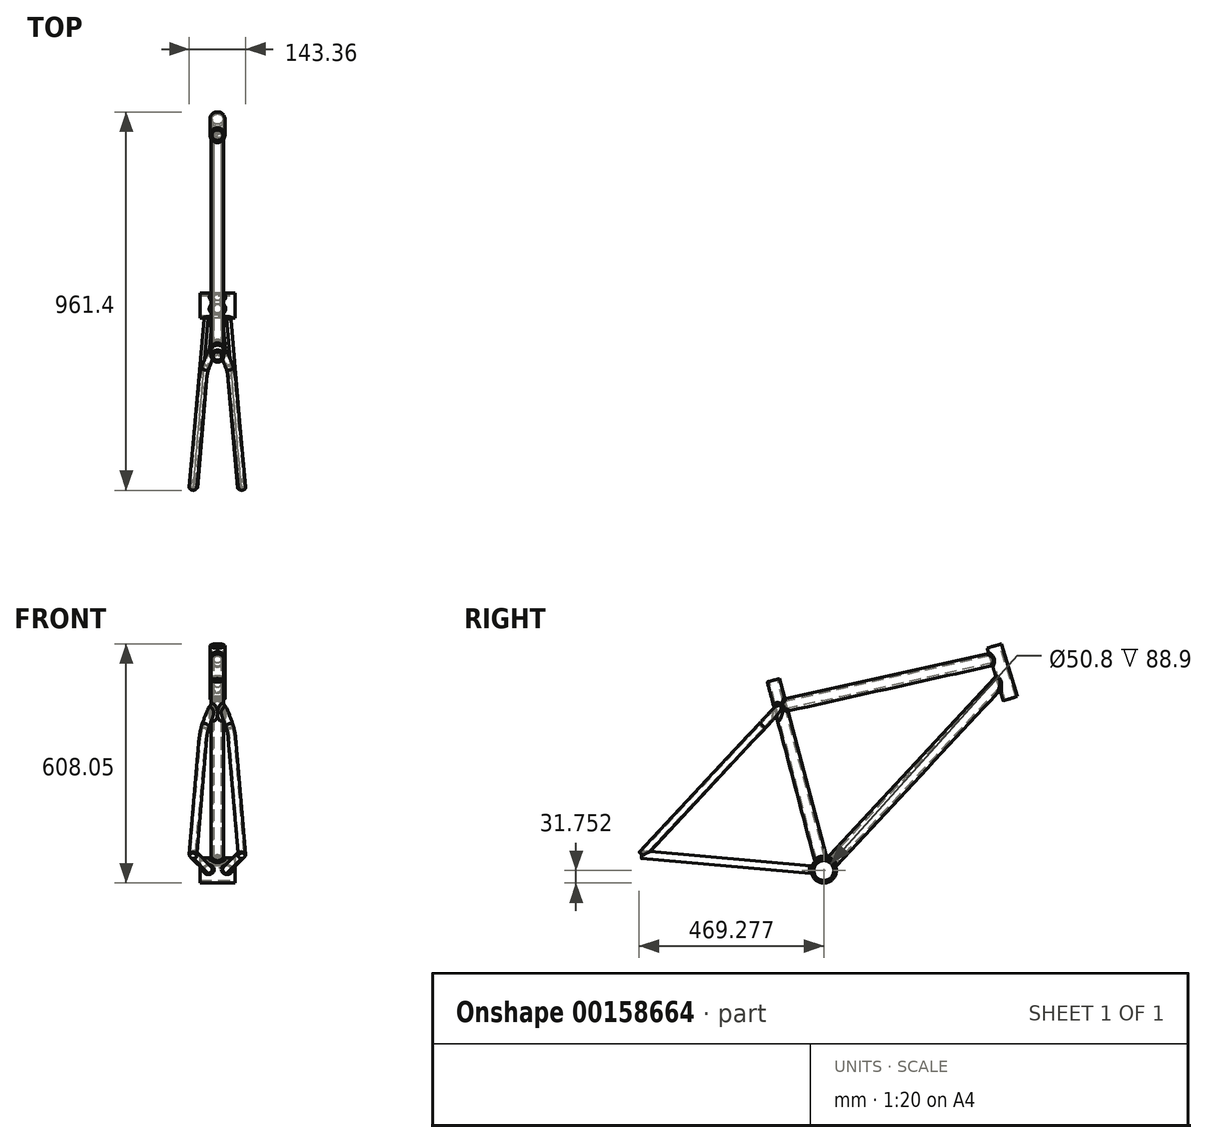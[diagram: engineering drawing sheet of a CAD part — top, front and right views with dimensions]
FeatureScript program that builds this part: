
annotation { "Feature Type Name" : "Feature", "Feature Type Description" : "" }
export const myFeature = defineFeature(function(context is Context, id is Id, definition is map)
    precondition{}
    {
        {
            var Q0;
            Q0=qCreatedBy(makeId("Right.planeOp"),FACE);
            var sketch = newSketch(context, id + "F0", { "sketchPlane" : qUnion([Q0])});
            skLineSegment(sketch, "E0", {"start": v(40.66, 113.91) * mm, "end": v(81.5, -19.68) * mm});
            skLineSegment(sketch, "E1.bottom", {"start": v(22.44, 108.34) * mm, "end": v(58.88, 119.48) * mm});
            skLineSegment(sketch, "E1.top", {"start": v(63.29, -25.25) * mm, "end": v(99.72, -14.11) * mm});
            skLineSegment(sketch, "E1.left", {"start": v(22.44, 108.34) * mm, "end": v(63.29, -25.25) * mm});
            skLineSegment(sketch, "E1.right", {"start": v(58.88, 119.48) * mm, "end": v(99.72, -14.11) * mm});
            skLineSegment(sketch, "E2", {"start": v(49.94, 83.55) * mm, "end": v(-503.21, -39.48) * mm});
            skLineSegment(sketch, "E3", {"start": v(-503.21, -39.48) * mm, "end": v(-392.4, -456.82) * mm});
            skLineSegment(sketch, "E4", {"start": v(-392.4, -456.82) * mm, "end": v(64.8, 34.97) * mm});
            skCircle(sketch, "E5", {"center": v(-392.4, -456.82) * mm, "radius": 31.75 * mm});
            skLineSegment(sketch, "E6", {"start": v(-503.21, -39.48) * mm, "end": v(-520.8, 26.74) * mm});
            skLineSegment(sketch, "E7", {"start": v(-520.8, 26.74) * mm, "end": v(-536.14, 22.67) * mm});
            skLineSegment(sketch, "E8.0", {"start": v(-536.14, 22.67) * mm, "end": v(-407.6, -461.46) * mm});
            skLineSegment(sketch, "E9", {"start": v(-407.6, -461.46) * mm, "end": v(-392.4, -456.82) * mm});
            skSolve(sketch);
        }
        {
            var Q0;
            {var subQ4=sQuery(id+"F0.wireOp",EDGE,"E6");Q0=makeQuery(id+"F0.imprint","IMPRINT",FACE,{"disambiguationData":[TD([[makeQuery(id+"F0.imprint","IMPRINT",EDGE,{"derivedFrom":subQ4}),1.0]])]});}
            var Q1;
            {var subQ0=sQuery(id+"F0.wireOp",EDGE,"E9");Q1=makeQuery(id+"F0.imprint","IMPRINT",FACE,{"disambiguationData":[TD([[makeQuery(id+"F0.imprint","IMPRINT",EDGE,{"derivedFrom":subQ0}),1.0]])]});}
            var Q2;
            Q2=sQuery(id+"F0.wireOp",EDGE,"E3");
            revolve(context, id + "F1", {"entities" : qUnion([Q0, Q1]), "axis" : qUnion([Q2]), "revolveType" : RevolveType.FULL});
        }
        {
            var Q0;
            {var subQ0=sQuery(id+"F0.wireOp",EDGE,"E2");var subQ1=sQuery(id+"F0.wireOp",EDGE,"E0");var subQ2=makeQuery(id+"F0.imprint","INTERSECT",VERTEX,{"derivedFrom":[subQ1,subQ0]});Q0=makeQuery(id+"F0.imprint","IMPRINT",FACE,{"disambiguationData":[TD([[makeQuery(id+"F0.imprint","IMPRINT",EDGE,{"disambiguationData":[TD([[subQ2,-1.0]])],"derivedFrom":subQ1}),-1.0]])]});}
            var Q1;
            {var subQ0=sQuery(id+"F0.wireOp",EDGE,"E1.bottom");var subQ1=sQuery(id+"F0.wireOp",EDGE,"E0");var subQ2=makeQuery(id+"F0.imprint","INTERSECT",VERTEX,{"derivedFrom":[subQ1,subQ0]});Q1=makeQuery(id+"F0.imprint","IMPRINT",FACE,{"disambiguationData":[TD([[makeQuery(id+"F0.imprint","IMPRINT",EDGE,{"disambiguationData":[TD([[subQ2,-1.0]])],"derivedFrom":subQ1}),-1.0]])]});}
            var Q2;
            {var subQ0=sQuery(id+"F0.wireOp",EDGE,"E1.top");var subQ1=sQuery(id+"F0.wireOp",EDGE,"E0");var subQ2=makeQuery(id+"F0.imprint","INTERSECT",VERTEX,{"derivedFrom":[subQ1,subQ0]});Q2=makeQuery(id+"F0.imprint","IMPRINT",FACE,{"disambiguationData":[TD([[makeQuery(id+"F0.imprint","IMPRINT",EDGE,{"disambiguationData":[TD([[subQ2,1.0]])],"derivedFrom":subQ1}),-1.0]])]});}
            var Q3;
            Q3=sQuery(id+"F0.wireOp",EDGE,"E0");
            revolve(context, id + "F2", {"entities" : qUnion([Q0, Q1, Q2]), "axis" : qUnion([Q3]), "revolveType" : RevolveType.FULL});
        }
        {
            var Q0;
            {var subQ0=sQuery(id+"F0.wireOp",EDGE,"E9");Q0=makeQuery(id+"F0.imprint","IMPRINT",FACE,{"disambiguationData":[TD([[makeQuery(id+"F0.imprint","IMPRINT",EDGE,{"derivedFrom":subQ0}),1.0]])]});}
            var Q1;
            {var subQ0=sQuery(id+"F0.wireOp",EDGE,"E4");var subQ3=sQuery(id+"F0.wireOp",EDGE,"E5");var subQ5=makeQuery(id+"F0.imprint","INTERSECT",VERTEX,{"derivedFrom":[subQ0,subQ3]});Q1=makeQuery(id+"F0.imprint","IMPRINT",FACE,{"disambiguationData":[TD([[makeQuery(id+"F0.imprint","IMPRINT",EDGE,{"disambiguationData":[TD([[subQ5,-1.0]])],"derivedFrom":subQ3}),1.0]])]});}
            var Q2;
            {var subQ0=sQuery(id+"F0.wireOp",EDGE,"E9");Q2=makeQuery(id+"F0.imprint","IMPRINT",FACE,{"disambiguationData":[TD([[makeQuery(id+"F0.imprint","IMPRINT",EDGE,{"derivedFrom":subQ0}),-1.0]])]});}
            var Q3;
            Q3=sQuery(id+"F0.wireOp",EDGE,"E5");
            extrude(context, id + "F3", {"entities" : qUnion([Q0, Q1, Q2]), "surfaceEntities" : qUnion([Q3]), "endBound" : BoundingType.SYMMETRIC, "depth" : 88.9 * mm});
        }
        {
            var Q0;
            Q0=sQuery(id+"F0.wireOp",VERTEX,"E2.start");
            var Q1;
            Q1=sQuery(id+"F0.wireOp",EDGE,"E2");
            cPlane(context, id + "F4", {"entities" : qUnion([Q0, Q1]), "cplaneType" : CPlaneType.LINE_POINT, "offset" : 25.4 * mm, "width" : 152.4 * mm, "height" : 152.4 * mm});
        }
        {
            var Q0;
            Q0=qCreatedBy(id+"F4.planeOp",FACE);
            var sketch = newSketch(context, id + "F5", { "sketchPlane" : qUnion([Q0])});
            skCircle(sketch, "E10", {"center": v(0, 70.71) * mm, "radius": 15.88 * mm});
            skCircle(sketch, "E11", {"center": v(0, 70.71) * mm, "radius": 9.52 * mm});
            skSolve(sketch);
        }
        {
            var Q0;
            Q0=makeQuery(id+"F5.imprint","IMPRINT",FACE,{"disambiguationData":[TD([[makeQuery(id+"F5.imprint","IMPRINT",EDGE,{"derivedFrom":sQuery(id+"F5.wireOp",EDGE,"E10")}),1.0]])]});
            var Q1;
            Q1=sQuery(id+"F0.wireOp",EDGE,"E2");
            sweep(context, id + "F6", {"operationType" : NewBodyOperationType.ADD, "profiles" : qUnion([Q0]), "path" : qUnion([Q1])});
        }
        {
            var Q0;
            Q0=sQuery(id+"F0.wireOp",VERTEX,"E4.end");
            var Q1;
            Q1=sQuery(id+"F0.wireOp",EDGE,"E4");
            cPlane(context, id + "F7", {"entities" : qUnion([Q0, Q1]), "cplaneType" : CPlaneType.LINE_POINT, "offset" : 25.4 * mm, "width" : 152.4 * mm, "height" : 152.4 * mm});
        }
        {
            var Q0;
            Q0=qCreatedBy(id+"F7.planeOp",FACE);
            var sketch = newSketch(context, id + "F8", { "sketchPlane" : qUnion([Q0])});
            skCircle(sketch, "E12", {"center": v(0, 23.65) * mm, "radius": 15.88 * mm});
            skCircle(sketch, "E13", {"center": v(0, 23.65) * mm, "radius": 9.52 * mm});
            skSolve(sketch);
        }
        {
            var Q0;
            Q0=makeQuery(id+"F8.imprint","IMPRINT",FACE,{"disambiguationData":[TD([[makeQuery(id+"F8.imprint","IMPRINT",EDGE,{"derivedFrom":sQuery(id+"F8.wireOp",EDGE,"E12")}),1.0]])]});
            var Q1;
            Q1=sQuery(id+"F0.wireOp",EDGE,"E4");
            sweep(context, id + "F9", {"operationType" : NewBodyOperationType.ADD, "profiles" : qUnion([Q0]), "path" : qUnion([Q1])});
        }
        {
            var Q0;
            Q0=qCreatedBy(makeId("Front.planeOp"),FACE);
            cPlane(context, id + "F10", {"entities" : qUnion([Q0]), "cplaneType" : CPlaneType.OFFSET, "offset" : 392.4 * mm, "width" : 152.4 * mm, "height" : 152.4 * mm});
        }
        {
            var Q0;
            Q0=qCreatedBy(id+"F10.planeOp",FACE);
            var sketch = newSketch(context, id + "F11", { "sketchPlane" : qUnion([Q0])});
            skLineSegment(sketch, "E14", {"start": v(44.45, -456.82) * mm, "end": v(-46.66, -456.82) * mm});
            skSolve(sketch);
        }
        {
            var Q0;
            Q0=qCreatedBy(id+"F10.planeOp",FACE);
            var Q1;
            Q1=sQuery(id+"F11.wireOp",EDGE,"E14");
            cPlane(context, id + "F12", {"entities" : qUnion([Q0, Q1]), "cplaneType" : CPlaneType.LINE_ANGLE, "offset" : 25.4 * mm, "angle" : 275 * degree, "width" : 152.4 * mm, "height" : 152.4 * mm});
        }
        {
            var Q0;
            Q0=qCreatedBy(id+"F12.planeOp",FACE);
            var sketch = newSketch(context, id + "F13", { "sketchPlane" : qUnion([Q0])});
            skLineSegment(sketch, "E15", {"start": v(33.46, -382.85) * mm, "end": v(23.9, -382.85) * mm});
            skLineSegment(sketch, "E16", {"start": v(30.7, -351.1) * mm, "end": v(71.02, -814.65) * mm});
            skLineSegment(sketch, "E17", {"start": v(0.57, -382.85) * mm, "end": v(0.57, -884.07) * mm});
            skLineSegment(sketch, "E18.0", {"start": v(21.14, -351.1) * mm, "end": v(61.53, -815.47) * mm});
            skLineSegment(sketch, "E19", {"start": v(71.02, -814.65) * mm, "end": v(61.53, -815.47) * mm});
            skLineSegment(sketch, "E20.MirrorCS", {"start": v(-20, -351.1) * mm, "end": v(-60.4, -815.47) * mm});
            skLineSegment(sketch, "E21.MirrorCS", {"start": v(-69.88, -814.65) * mm, "end": v(-60.4, -815.47) * mm});
            skLineSegment(sketch, "E22.MirrorCS", {"start": v(-29.56, -351.1) * mm, "end": v(-69.88, -814.65) * mm});
            skLineSegment(sketch, "E23", {"start": v(30.7, -351.1) * mm, "end": v(21.14, -351.1) * mm});
            skPoint(sketch, "E24.orphan", {"position": v(33.46, -382.85) * mm});
            skPoint(sketch, "E25.orphan", {"position": v(23.9, -382.85) * mm});
            skPoint(sketch, "E26.orphan", {"position": v(-32.32, -382.85) * mm});
            skPoint(sketch, "E27.orphan", {"position": v(-22.76, -382.85) * mm});
            skPoint(sketch, "E28.trimOffspring.end.orphan", {"position": v(-44.45, -382.85) * mm});
            skLineSegment(sketch, "E29.trimOffspring", {"start": v(-20, -351.1) * mm, "end": v(-29.56, -351.1) * mm});
            skPoint(sketch, "E30.orphan", {"position": v(45.59, -382.85) * mm});
            skSolve(sketch);
        }
        {
            var Q0;
            {var subQ0=sQuery(id+"F13.wireOp",EDGE,"E16");Q0=makeQuery(id+"F13.imprint","IMPRINT",FACE,{"disambiguationData":[TD([[makeQuery(id+"F13.imprint","IMPRINT",EDGE,{"derivedFrom":subQ0}),-1.0]])]});}
            var Q1;
            Q1=sQuery(id+"F13.wireOp",EDGE,"E18.0");
            revolve(context, id + "F14", {"operationType" : NewBodyOperationType.ADD, "entities" : qUnion([Q0]), "axis" : qUnion([Q1]), "revolveType" : RevolveType.FULL});
        }
        {
            var Q0;
            Q0=makeQuery(id+"F13.imprint","IMPRINT",FACE,{"disambiguationData":[TD([[makeQuery(id+"F13.imprint","IMPRINT",EDGE,{"derivedFrom":sQuery(id+"F13.wireOp",EDGE,"E20.MirrorCS")}),-1.0]])]});
            var Q1;
            Q1=sQuery(id+"F13.wireOp",EDGE,"E20.MirrorCS");
            revolve(context, id + "F15", {"operationType" : NewBodyOperationType.ADD, "entities" : qUnion([Q0]), "axis" : qUnion([Q1]), "revolveType" : RevolveType.FULL});
        }
        {
            var Q0;
            Q0=sQuery(id+"F13.wireOp",VERTEX,"E19.end");
            var Q1;
            Q1=sQuery(id+"F0.wireOp",VERTEX,"E3.start");
            var Q2;
            Q2=sQuery(id+"F13.wireOp",VERTEX,"E20.MirrorCS.end");
            cPlane(context, id + "F16", {"entities" : qUnion([Q0, Q1, Q2]), "cplaneType" : CPlaneType.THREE_POINT, "offset" : 25.4 * mm, "width" : 152.4 * mm, "height" : 152.4 * mm});
        }
        {
            var Q0;
            Q0=qCreatedBy(id+"F16.planeOp",FACE);
            var sketch = newSketch(context, id + "F17", { "sketchPlane" : qUnion([Q0])});
            skPoint(sketch, "E31.0", {"position": v(-61.53, -887.79) * mm});
            skPoint(sketch, "E32.0", {"position": v(60.4, -887.79) * mm});
            skPoint(sketch, "E33.0", {"position": v(0, -372.24) * mm});
            skLineSegment(sketch, "E34", {"start": v(-36.13, -481.84) * mm, "end": v(-61.53, -887.79) * mm});
            skLineSegment(sketch, "E35", {"start": v(51.14, -372.24) * mm, "end": v(-6.35, -372.24) * mm});
            skPoint(sketch, "E36.visualSharp", {"position": v(-34.83, -461.14) * mm});
            skArc(sketch, "E36.filletArc", {"start": v(-30.2, -440.93) * mm, "mid": v(-34, -461.26) * mm, "end": v(-36.13, -481.84) * mm});
            skFitSpline(sketch, "E37", {"points": [v(-30.2, -440.93) * mm, v(-19.06, -399.88) * mm, v(-12.73, -381.3) * mm, v(-6.35, -372.24) * mm], "startDerivative": vector(26.27, 97.47) * mm, "endDerivative": vector(29.13, 35.48) * mm});
            skSolve(sketch);
        }
        {
            var Q0;
            Q0=sQuery(id+"F17.wireOp",VERTEX,"E31.0");
            var Q1;
            Q1=sQuery(id+"F17.wireOp",EDGE,"E34");
            cPlane(context, id + "F18", {"entities" : qUnion([Q0, Q1]), "cplaneType" : CPlaneType.LINE_POINT, "offset" : 25.4 * mm, "width" : 152.4 * mm, "height" : 152.4 * mm});
        }
        {
            var Q0;
            Q0=qCreatedBy(id+"F18.planeOp",FACE);
            var sketch = newSketch(context, id + "F19", { "sketchPlane" : qUnion([Q0])});
            skCircle(sketch, "E38", {"center": v(6.6, 340.53) * mm, "radius": 9.53 * mm});
            skCircle(sketch, "E39", {"center": v(6.6, 340.53) * mm, "radius": 6.35 * mm});
            skSolve(sketch);
        }
        {
            var Q0;
            Q0=makeQuery(id+"F19.imprint","IMPRINT",FACE,{"disambiguationData":[TD([[makeQuery(id+"F19.imprint","IMPRINT",EDGE,{"derivedFrom":sQuery(id+"F19.wireOp",EDGE,"E38")}),1.0]])]});
            var Q1;
            Q1=sQuery(id+"F17.wireOp",EDGE,"E34");
            var Q2;
            Q2=sQuery(id+"F17.wireOp",EDGE,"E36.filletArc");
            var Q3;
            Q3=sQuery(id+"F17.wireOp",EDGE,"E37");
            sweep(context, id + "F20", {"operationType" : NewBodyOperationType.ADD, "profiles" : qUnion([Q0]), "path" : qUnion([Q1, Q2, Q3])});
        }
        {
            var Q0;
            Q0=makeQuery(id+"F1.opRevolve","SWEPT_BODY",BODY,{"disambiguationData":[OSD([sQuery(id+"F0.wireOp",EDGE,"E3"),sQuery(id+"F0.wireOp",EDGE,"E6"),sQuery(id+"F0.wireOp",EDGE,"E7"),sQuery(id+"F0.wireOp",EDGE,"E8.0"),sQuery(id+"F0.wireOp",EDGE,"E9")])]});
            var Q1;
            Q1=qCreatedBy(makeId("Right.planeOp"),FACE);
            mirror(context, id + "F21", {"operationType" : NewBodyOperationType.ADD, "entities" : qUnion([Q0]), "mirrorPlane" : qUnion([Q1])});
        }
        {
            var Q0;
            Q0=makeQuery(id+"F3.opExtrude","CAP_FACE",FACE,{"disambiguationData":[OSD([sQuery(id+"F0.wireOp",EDGE,"E5")])],"isStart":false});
            var sketch = newSketch(context, id + "F22", { "sketchPlane" : qUnion([Q0])});
            skCircle(sketch, "E40.0", {"center": v(-392.4, -456.82) * mm, "radius": 31.75 * mm});
            skCircle(sketch, "E41.0", {"center": v(-392.4, -456.82) * mm, "radius": 25.4 * mm});
            skSolve(sketch);
        }
        {
            var Q0;
            Q0=makeQuery(id+"F22.imprint","IMPRINT",FACE,{"disambiguationData":[TD([[makeQuery(id+"F22.imprint","IMPRINT",EDGE,{"derivedFrom":sQuery(id+"F22.wireOp",EDGE,"E41.0")}),1.0]])]});
            extrude(context, id + "F23", {"entities" : qUnion([Q0]), "operationType" : NewBodyOperationType.REMOVE, "endBound" : BoundingType.THROUGH_ALL, "oppositeDirection" : true, "depth" : 25.4 * mm});
        }
        {
            var Q0;
            Q0=makeQuery(id+"F1.opRevolve","SWEPT_FACE",FACE,{"disambiguationData":[OSD([sQuery(id+"F0.wireOp",EDGE,"E7")])]});
            var sketch = newSketch(context, id + "F24", { "sketchPlane" : qUnion([Q0])});
            skCircle(sketch, "E42.0", {"center": v(0, -496.5) * mm, "radius": 15.87 * mm});
            skCircle(sketch, "E43", {"center": v(0, -496.5) * mm, "radius": 10.8 * mm});
            skSolve(sketch);
        }
        {
            var Q0;
            Q0=makeQuery(id+"F24.imprint","IMPRINT",FACE,{"disambiguationData":[TD([[makeQuery(id+"F24.imprint","IMPRINT",EDGE,{"derivedFrom":sQuery(id+"F24.wireOp",EDGE,"E43")}),1.0]])]});
            var Q1;
            Q1=makeQuery(id+"F3.opExtrude","SWEPT_FACE",FACE,{"disambiguationData":[OSD([sQuery(id+"F0.wireOp",EDGE,"E5")])]});
            extrude(context, id + "F25", {"entities" : qUnion([Q0]), "operationType" : NewBodyOperationType.REMOVE, "endBound" : BoundingType.UP_TO_SURFACE, "oppositeDirection" : true, "endBoundEntityFace" : qUnion([Q1]), "depth" : 25.4 * mm});
        }
        {
            var Q0;
            Q0=makeQuery(id+"F2.opRevolve","SWEPT_FACE",FACE,{"disambiguationData":[OSD([sQuery(id+"F0.wireOp",EDGE,"E1.bottom")])]});
            var sketch = newSketch(context, id + "F26", { "sketchPlane" : qUnion([Q0])});
            skCircle(sketch, "E44", {"center": v(0, 72.19) * mm, "radius": 13.97 * mm});
            skSolve(sketch);
        }
        {
            var Q0;
            Q0=makeQuery(id+"F26.imprint","IMPRINT",FACE,{"disambiguationData":[TD([[makeQuery(id+"F26.imprint","IMPRINT",EDGE,{"derivedFrom":sQuery(id+"F26.wireOp",EDGE,"E44")}),1.0]])]});
            extrude(context, id + "F27", {"entities" : qUnion([Q0]), "operationType" : NewBodyOperationType.REMOVE, "endBound" : BoundingType.THROUGH_ALL, "oppositeDirection" : true, "depth" : 25.4 * mm});
        }
        {
            var Q0;
            Q0=makeQuery(id+"F6.boolean.opBoolean","INTERSECT",EDGE,{"disambiguationData":[OD(1.0)],"derivedFrom":[makeQuery(id+"F1.opRevolve","SWEPT_FACE",FACE,{"disambiguationData":[OSD([sQuery(id+"F0.wireOp",EDGE,"E8.0")])]}),makeQuery(id+"F6.opSweep","SWEPT_FACE",FACE,{"disambiguationData":[OSD([sQuery(id+"F0.wireOp",EDGE,"E2"),sQuery(id+"F5.wireOp",EDGE,"E10")])]})]});
            var Q1;
            Q1=makeQuery(id+"F6.boolean.opBoolean","INTERSECT",EDGE,{"disambiguationData":[OD(0.0)],"derivedFrom":[makeQuery(id+"F1.opRevolve","SWEPT_FACE",FACE,{"disambiguationData":[OSD([sQuery(id+"F0.wireOp",EDGE,"E8.0")])]}),makeQuery(id+"F6.opSweep","SWEPT_FACE",FACE,{"disambiguationData":[OSD([sQuery(id+"F0.wireOp",EDGE,"E2"),sQuery(id+"F5.wireOp",EDGE,"E10")])]})]});
            var Q2;
            Q2=makeQuery(id+"F9.boolean.opBoolean","INTERSECT",EDGE,{"derivedFrom":[makeQuery(id+"F3.opExtrude","SWEPT_FACE",FACE,{"disambiguationData":[OSD([sQuery(id+"F0.wireOp",EDGE,"E5")])]}),makeQuery(id+"F9.opSweep","SWEPT_FACE",FACE,{"disambiguationData":[OSD([sQuery(id+"F0.wireOp",EDGE,"E4"),sQuery(id+"F8.wireOp",EDGE,"E12")])]})]});
            var Q3;
            Q3=makeQuery(id+"F9.boolean.opBoolean","INTERSECT",EDGE,{"derivedFrom":[makeQuery(id+"F3.opExtrude","SWEPT_FACE",FACE,{"disambiguationData":[OSD([sQuery(id+"F0.wireOp",EDGE,"E5")])]}),makeQuery(id+"F6.boolean.opBoolean","SPLIT",FACE,{"disambiguationData":[TD([makeQuery(id+"F1.opRevolve","SWEPT_FACE",FACE,{"disambiguationData":[OSD([sQuery(id+"F0.wireOp",EDGE,"E7")])]})])],"derivedFrom":makeQuery(id+"F1.opRevolve","SWEPT_FACE",FACE,{"disambiguationData":[OSD([sQuery(id+"F0.wireOp",EDGE,"E8.0")])]})})]});
            var Q4;
            {var subQ0=sQuery(id+"F0.wireOp",EDGE,"E5");Q4=makeQuery(id+"F14.boolean.opBoolean","INTERSECT",EDGE,{"derivedFrom":[makeQuery(id+"F9.boolean.opBoolean","SPLIT",FACE,{"disambiguationData":[TD([makeQuery(id+"F1.opRevolve","SWEPT_FACE",FACE,{"disambiguationData":[OSD([sQuery(id+"F0.wireOp",EDGE,"E8.0")])]})])],"derivedFrom":makeQuery(id+"F3.opExtrude","SWEPT_FACE",FACE,{"disambiguationData":[OSD([subQ0])]})}),makeQuery(id+"F14.opRevolve","SWEPT_FACE",FACE,{"disambiguationData":[OSD([sQuery(id+"F13.wireOp",EDGE,"E16")])]})]});}
            var Q5;
            {var subQ0=sQuery(id+"F0.wireOp",EDGE,"E5");Q5=makeQuery(id+"F15.boolean.opBoolean","INTERSECT",EDGE,{"derivedFrom":[makeQuery(id+"F9.boolean.opBoolean","SPLIT",FACE,{"disambiguationData":[TD([makeQuery(id+"F1.opRevolve","SWEPT_FACE",FACE,{"disambiguationData":[OSD([sQuery(id+"F0.wireOp",EDGE,"E8.0")])]})])],"derivedFrom":makeQuery(id+"F3.opExtrude","SWEPT_FACE",FACE,{"disambiguationData":[OSD([subQ0])]})}),makeQuery(id+"F15.opRevolve","SWEPT_FACE",FACE,{"disambiguationData":[OSD([sQuery(id+"F13.wireOp",EDGE,"E22.MirrorCS")])]})]});}
            var Q6;
            {var subQ0=sQuery(id+"F0.wireOp",EDGE,"E5");Q6=makeQuery(id+"F21.opPattern","COPY",EDGE,{"derivedFrom":makeQuery(id+"F14.boolean.opBoolean","INTERSECT",EDGE,{"derivedFrom":[makeQuery(id+"F9.boolean.opBoolean","SPLIT",FACE,{"disambiguationData":[TD([makeQuery(id+"F1.opRevolve","SWEPT_FACE",FACE,{"disambiguationData":[OSD([sQuery(id+"F0.wireOp",EDGE,"E8.0")])]})])],"derivedFrom":makeQuery(id+"F3.opExtrude","SWEPT_FACE",FACE,{"disambiguationData":[OSD([subQ0])]})}),makeQuery(id+"F14.opRevolve","SWEPT_FACE",FACE,{"disambiguationData":[OSD([sQuery(id+"F13.wireOp",EDGE,"E16")])]})]}),"instanceName":"1"});}
            var Q7;
            {var subQ0=sQuery(id+"F0.wireOp",EDGE,"E5");Q7=makeQuery(id+"F21.opPattern","COPY",EDGE,{"derivedFrom":makeQuery(id+"F15.boolean.opBoolean","INTERSECT",EDGE,{"derivedFrom":[makeQuery(id+"F9.boolean.opBoolean","SPLIT",FACE,{"disambiguationData":[TD([makeQuery(id+"F1.opRevolve","SWEPT_FACE",FACE,{"disambiguationData":[OSD([sQuery(id+"F0.wireOp",EDGE,"E8.0")])]})])],"derivedFrom":makeQuery(id+"F3.opExtrude","SWEPT_FACE",FACE,{"disambiguationData":[OSD([subQ0])]})}),makeQuery(id+"F15.opRevolve","SWEPT_FACE",FACE,{"disambiguationData":[OSD([sQuery(id+"F13.wireOp",EDGE,"E22.MirrorCS")])]})]}),"instanceName":"1"});}
            var Q8;
            Q8=makeQuery(id+"F9.boolean.opBoolean","INTERSECT",EDGE,{"derivedFrom":[makeQuery(id+"F6.boolean.opBoolean","SPLIT",FACE,{"disambiguationData":[TD([makeQuery(id+"F1.opRevolve","SWEPT_FACE",FACE,{"disambiguationData":[OSD([sQuery(id+"F0.wireOp",EDGE,"E7")])]})])],"derivedFrom":makeQuery(id+"F1.opRevolve","SWEPT_FACE",FACE,{"disambiguationData":[OSD([sQuery(id+"F0.wireOp",EDGE,"E8.0")])]})}),makeQuery(id+"F9.opSweep","SWEPT_FACE",FACE,{"disambiguationData":[OSD([sQuery(id+"F0.wireOp",EDGE,"E4"),sQuery(id+"F8.wireOp",EDGE,"E12")])]})]});
            var Q9;
            Q9=makeQuery(id+"F9.boolean.opBoolean","INTERSECT",EDGE,{"derivedFrom":[makeQuery(id+"F6.boolean.opBoolean","SPLIT",FACE,{"disambiguationData":[TD([makeQuery(id+"F2.opRevolve","SWEPT_FACE",FACE,{"disambiguationData":[OSD([sQuery(id+"F0.wireOp",EDGE,"E1.bottom")])]})])],"derivedFrom":makeQuery(id+"F2.opRevolve","SWEPT_FACE",FACE,{"disambiguationData":[OSD([sQuery(id+"F0.wireOp",EDGE,"E1.left")])]})}),makeQuery(id+"F9.opSweep","SWEPT_FACE",FACE,{"disambiguationData":[OSD([sQuery(id+"F0.wireOp",EDGE,"E4"),sQuery(id+"F8.wireOp",EDGE,"E12")])]})]});
            var Q10;
            Q10=makeQuery(id+"F6.boolean.opBoolean","INTERSECT",EDGE,{"derivedFrom":[makeQuery(id+"F2.opRevolve","SWEPT_FACE",FACE,{"disambiguationData":[OSD([sQuery(id+"F0.wireOp",EDGE,"E1.left")])]}),makeQuery(id+"F6.opSweep","SWEPT_FACE",FACE,{"disambiguationData":[OSD([sQuery(id+"F0.wireOp",EDGE,"E2"),sQuery(id+"F5.wireOp",EDGE,"E10")])]})]});
            fillet(context, id + "F28", {"entities" : qUnion([Q0, Q1, Q2, Q3, Q4, Q5, Q6, Q7, Q8, Q9, Q10]), "radius" : 5.08 * mm, "tangentPropagation" : true, "allowEdgeOverflow" : false});
        }
        {
            var Q0;
            Q0=makeQuery(id+"F20.boolean.opBoolean","INTERSECT",EDGE,{"derivedFrom":[makeQuery(id+"F6.boolean.opBoolean","SPLIT",FACE,{"disambiguationData":[TD([makeQuery(id+"F1.opRevolve","SWEPT_FACE",FACE,{"disambiguationData":[OSD([sQuery(id+"F0.wireOp",EDGE,"E7")])]})])],"derivedFrom":makeQuery(id+"F1.opRevolve","SWEPT_FACE",FACE,{"disambiguationData":[OSD([sQuery(id+"F0.wireOp",EDGE,"E8.0")])]})}),makeQuery(id+"F20.opSweep","SWEPT_FACE",FACE,{"disambiguationData":[OSD([sQuery(id+"F17.wireOp",EDGE,"E37"),sQuery(id+"F19.wireOp",EDGE,"E38")])]})]});
            var Q1;
            Q1=makeQuery(id+"F21.opPattern","COPY",EDGE,{"derivedFrom":makeQuery(id+"F20.boolean.opBoolean","INTERSECT",EDGE,{"derivedFrom":[makeQuery(id+"F6.boolean.opBoolean","SPLIT",FACE,{"disambiguationData":[TD([makeQuery(id+"F1.opRevolve","SWEPT_FACE",FACE,{"disambiguationData":[OSD([sQuery(id+"F0.wireOp",EDGE,"E7")])]})])],"derivedFrom":makeQuery(id+"F1.opRevolve","SWEPT_FACE",FACE,{"disambiguationData":[OSD([sQuery(id+"F0.wireOp",EDGE,"E8.0")])]})}),makeQuery(id+"F20.opSweep","SWEPT_FACE",FACE,{"disambiguationData":[OSD([sQuery(id+"F17.wireOp",EDGE,"E37"),sQuery(id+"F19.wireOp",EDGE,"E38")])]})]}),"instanceName":"1"});
            fillet(context, id + "F29", {"entities" : qUnion([Q0, Q1]), "radius" : 10.16 * mm, "tangentPropagation" : true, "allowEdgeOverflow" : false});
        }
    });
